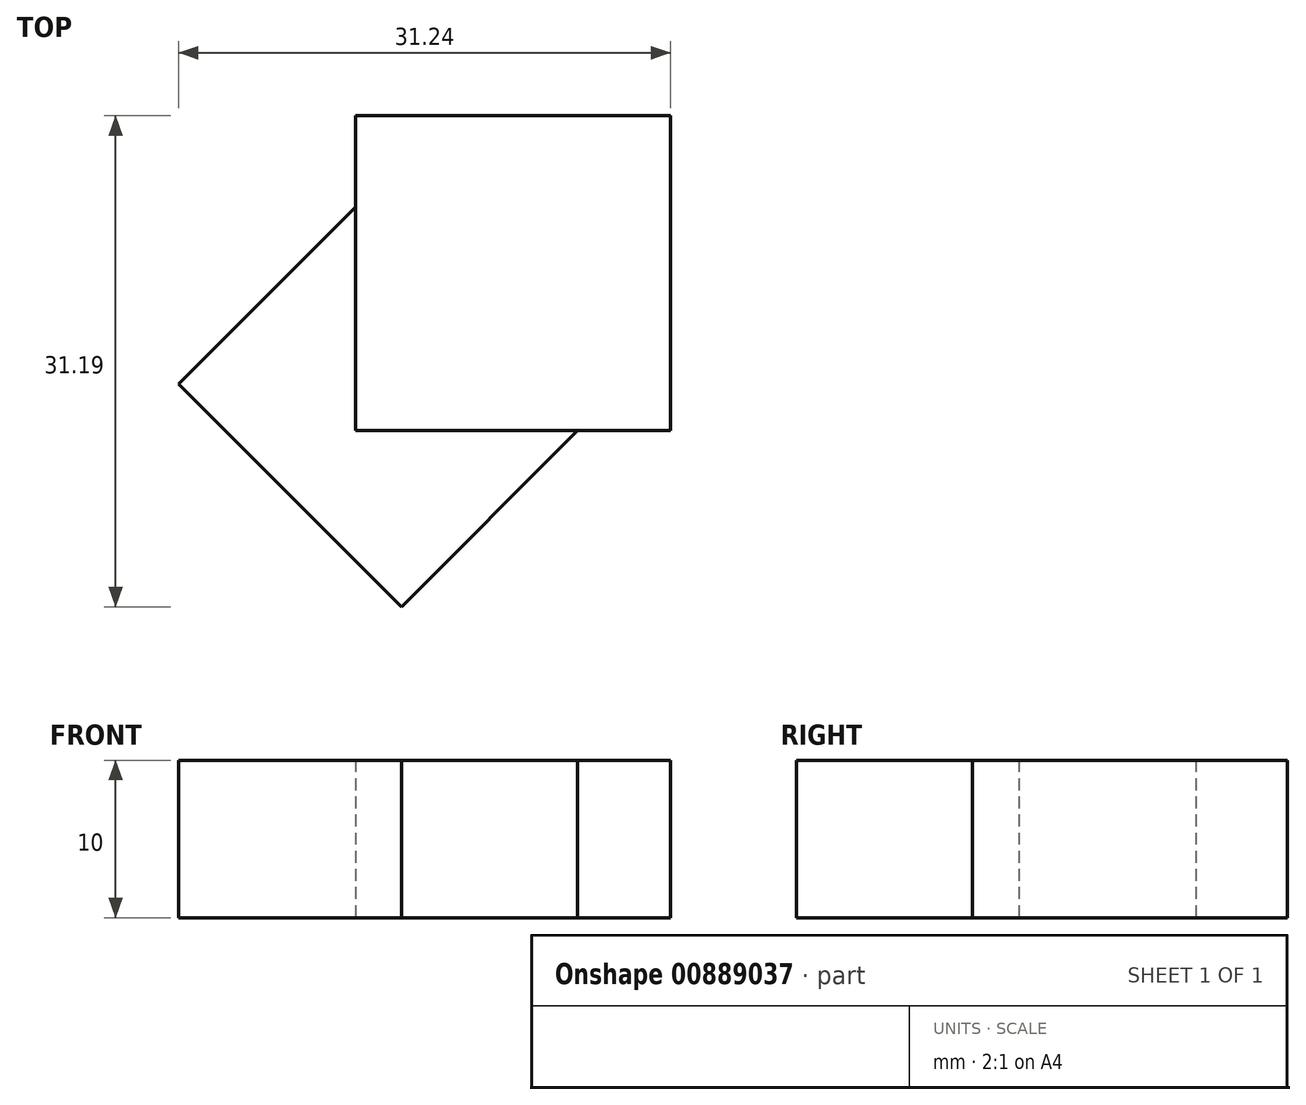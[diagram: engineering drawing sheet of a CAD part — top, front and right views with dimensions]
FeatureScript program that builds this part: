
annotation { "Feature Type Name" : "Feature", "Feature Type Description" : "" }
export const myFeature = defineFeature(function(context is Context, id is Id, definition is map)
    precondition{}
    {
        {
            var Q0;
            Q0=qCreatedBy(makeId("Top.planeOp"),FACE);
            var sketch = newSketch(context, id + "F0", { "sketchPlane" : qUnion([Q0])});
            skLineSegment(sketch, "E0.top", {"start": v(0, 20) * mm, "end": v(20, 20) * mm});
            skLineSegment(sketch, "E0.left", {"start": v(0, 0) * mm, "end": v(0, 20) * mm});
            skLineSegment(sketch, "E0.right", {"start": v(20, 0) * mm, "end": v(20, 20) * mm});
            skLineSegment(sketch, "E1", {"start": v(20, 20) * mm, "end": v(0, 0) * mm});
            skLineSegment(sketch, "E2", {"start": v(0, 20) * mm, "end": v(20, 0) * mm});
            skLineSegment(sketch, "E3", {"start": v(0, 0) * mm, "end": v(20, 0) * mm});
            skLineSegment(sketch, "E4", {"start": v(2.9, 17.1) * mm, "end": v(-11.24, 2.95) * mm});
            skLineSegment(sketch, "E5", {"start": v(-11.24, 2.95) * mm, "end": v(2.9, -11.19) * mm});
            skLineSegment(sketch, "E6", {"start": v(2.9, -11.19) * mm, "end": v(17.05, 2.95) * mm});
            skPoint(sketch, "E7", {"position": v(10, 10) * mm});
            skLineSegment(sketch, "E8", {"start": v(0, 20) * mm, "end": v(10, 10) * mm});
            skSolve(sketch);
        }
        {
            var Q0;
            {var subQ0=sQuery(id+"F0.wireOp",EDGE,"E0.top");Q0=makeQuery(id+"F0.imprint","IMPRINT",FACE,{"disambiguationData":[TD([[makeQuery(id+"F0.imprint","IMPRINT",EDGE,{"derivedFrom":subQ0}),-1.0]])]});}
            var Q1;
            {var subQ3=sQuery(id+"F0.wireOp",EDGE,"E4");var subQ5=sQuery(id+"F0.wireOp",EDGE,"E8");var subQ7=makeQuery(id+"F0.imprint","INTERSECT",VERTEX,{"derivedFrom":[subQ3,subQ5]});Q1=makeQuery(id+"F0.imprint","IMPRINT",FACE,{"disambiguationData":[TD([[makeQuery(id+"F0.imprint","IMPRINT",EDGE,{"disambiguationData":[TD([[subQ7,-1.0]])],"derivedFrom":subQ3}),1.0]])]});}
            var Q2;
            {var subQ0=sQuery(id+"F0.wireOp",EDGE,"E8");var subQ3=sQuery(id+"F0.wireOp",EDGE,"E4");var subQ5=makeQuery(id+"F0.imprint","INTERSECT",VERTEX,{"derivedFrom":[subQ3,subQ0]});Q2=makeQuery(id+"F0.imprint","IMPRINT",FACE,{"disambiguationData":[TD([[makeQuery(id+"F0.imprint","IMPRINT",EDGE,{"disambiguationData":[TD([[subQ5,-1.0]])],"derivedFrom":subQ3}),-1.0]])]});}
            var Q3;
            {var subQ3=sQuery(id+"F0.wireOp",EDGE,"E2");var subQ5=sQuery(id+"F0.wireOp",EDGE,"E6");var subQ6=makeQuery(id+"F0.imprint","INTERSECT",VERTEX,{"derivedFrom":[subQ3,subQ5]});Q3=makeQuery(id+"F0.imprint","IMPRINT",FACE,{"disambiguationData":[TD([[makeQuery(id+"F0.imprint","IMPRINT",EDGE,{"disambiguationData":[TD([[subQ6,1.0]])],"derivedFrom":subQ5}),1.0]])]});}
            var Q4;
            {var subQ1=sQuery(id+"F0.wireOp",EDGE,"E2");var subQ3=sQuery(id+"F0.wireOp",EDGE,"E6");var subQ4=makeQuery(id+"F0.imprint","INTERSECT",VERTEX,{"derivedFrom":[subQ1,subQ3]});Q4=makeQuery(id+"F0.imprint","IMPRINT",FACE,{"disambiguationData":[TD([[makeQuery(id+"F0.imprint","IMPRINT",EDGE,{"disambiguationData":[TD([[subQ4,1.0]])],"derivedFrom":subQ3}),-1.0]])]});}
            var Q5;
            {var subQ0=sQuery(id+"F0.wireOp",EDGE,"E0.right");Q5=makeQuery(id+"F0.imprint","IMPRINT",FACE,{"disambiguationData":[TD([[makeQuery(id+"F0.imprint","IMPRINT",EDGE,{"derivedFrom":subQ0}),1.0]])]});}
            extrude(context, id + "F1", {"entities" : qUnion([Q0, Q1, Q2, Q3, Q4, Q5]), "depth" : 10 * mm, "offsetDistance" : 25 * mm});
        }
        {
            var Q0;
            {var subQ0=sQuery(id+"F0.wireOp",EDGE,"E5");Q0=makeQuery(id+"F0.imprint","IMPRINT",FACE,{"disambiguationData":[TD([[makeQuery(id+"F0.imprint","IMPRINT",EDGE,{"derivedFrom":subQ0}),1.0]])]});}
            extrude(context, id + "F2", {"entities" : qUnion([Q0]), "depth" : 10 * mm, "offsetDistance" : 25 * mm});
        }
    });
